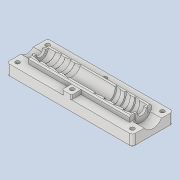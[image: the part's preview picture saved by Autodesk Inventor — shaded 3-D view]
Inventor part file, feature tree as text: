
AUTODESK INVENTOR PART (.ipt)
format: ipt  version: 2020.4 (Build 244396000, 396)  size: 515,072 bytes
history: native  units: mm
features: sketch x14, extrude x13, projected_geometry x9, fillet x3, other x1, mirror x1, boolean_combine x1, chamfer x1
ambient origin geometry x8: Origin, YZ Plane, XZ Plane, XY Plane, X Axis, Y Axis, Z Axis, Center Point
bodies: Volumenkörper1 (feature_tree), Solid2 (feature_tree), Solid3 (feature_tree)
feature tree (43):
  extrude  "Extrusion1"  Depth=6.0mm
  other  "Spirale1"
  mirror  "Spiegeln1"
  extrude  "Extrusion5"  Depth=10.0mm
  extrude  "Extrusion6"  Depth=1.0mm
  boolean_combine  "Combine1"
  extrude  "Extrusion7"  Depth=10.0mm TaperAngle=0.0deg
  extrude  "Extrusion8"  Depth=7.0mm TaperAngle=0.0deg
  extrude  "Extrusion9"  Depth=24.0mm
  extrude  "Extrusion10"  Depth=12.0mm TaperAngle=0.0deg
  extrude  "Extrusion11"  Depth=74.0mm
  chamfer  "Chamfer2"  Distance=4.0mm
  extrude  "Extrusion12"  Depth=3.0mm
  fillet  "Fillet1"  Radius=3.0mm
  extrude  "Extrusion13"  Depth=3.0mm
  fillet  "Fillet2"  Radius=4.0mm
  extrude  "Extrusion14"  Depth=7.0mm
  extrude  "Extrusion15"  Depth=7.0mm
  extrude  "Extrusion17"  Depth=7.0mm
  fillet  "Fillet3"  Radius=4.0mm
  sketch  "Skizze1"  dims[d0=6.0mm d1=11.0mm]
  sketch  "Skizze3"  dims[d2=36.0mm d3=0.0mm]
  projected_geometry  "Projizierte Kontur2"
  sketch  "Sketch7"  dims[d8=7.0mm d9=24.5mm d10=10.0mm d11=0.0mm d12=90.0deg d13=90.0deg d14=0.0mm d15=0.0mm d16=4.0mm]
  sketch  "Sketch8"  dims[d17=13.962634mm d18=1.0mm]
  sketch  "Sketch9"  dims[d19=0.1mm d32=10.0mm d33=0.0mm]
  projected_geometry  "Projected Loop4"
  sketch  "Sketch10"  dims[d34=7.0mm d35=100.0mm d36=0.0mm]
  projected_geometry  "Projected Loop5"
  projected_geometry  "Projected Loop6"
  projected_geometry  "Projected Loop7"
  projected_geometry  "Projected Loop8"
  sketch  "Sketch11"  dims[d37=82.0mm d38=0.0mm d39=24.0mm]
  projected_geometry  "Projected Loop9"
  sketch  "Sketch12"  dims[d40=30.0mm d41=12.0mm d42=0.0mm]
  sketch  "Sketch13"  dims[d43=74.0mm d44=16.0mm]
  projected_geometry  "Projected Loop10"
  projected_geometry  "Projected Loop11"
  sketch  "Sketch14"  dims[d45=79.0mm]
  sketch  "Sketch15"  dims[d46=21.0mm d47=4.0mm d48=0.0mm]
  sketch  "Sketch16"  dims[d49=3.0mm d50=3.0mm d51=3.0mm]
  sketch  "Sketch17"  dims[d52=3.0mm d53=4.0mm d54=4.0mm]
  sketch  "Sketch19"  dims[d55=4.0mm d56=4.0mm d57=4.0mm d58=4.0mm d59=4.0mm d60=4.0mm d61=10.0mm d62=0.0mm d63=1.0mm d64=1.0mm d65=1.0mm d66=1.0mm d67=6.0mm d68=10.0mm d69=0.0mm d70=10.0mm d71=0.0mm d72=1.0mm d73=2.0mm d74=45.0deg d75=3.0mm d76=3.0mm d77=4.0mm d78=46.0mm d79=4.0mm d80=44.0mm d81=5.5mm d82=5.5mm d83=5.5mm d84=5.5mm d85=5.5mm d86=5.5mm d87=5.0mm d88=0.0mm d89=2.0mm d90=0.5mm d91=6.5mm d92=74.1mm d93=2.1mm d94=0.0mm d95=0.0mm d96=1.0mm d97=12.0mm d98=0.2mm d99=7.9mm d100=0.0mm d101=0.0mm d102=15.0mm d103=0.2mm d104=7.9mm d105=0.0mm d106=0.0mm d110=3.0mm d111=0.0mm d115=1.0mm d116=0.0mm d117=0.0mm d118=7.0mm]
